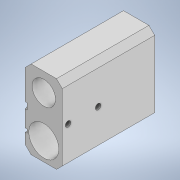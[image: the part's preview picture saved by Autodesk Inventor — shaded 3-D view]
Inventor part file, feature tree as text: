
AUTODESK INVENTOR PART (.ipt)
format: ipt  version: 2022 (Build 260153000, 153)  size: 282,624 bytes
history: native  units: in
note: dims shown in document units (in); Inventor stores cm internally (conversion verified against a paired STEP export)
features: extrude x5, sketch x4, projected_geometry x3, chamfer x1, fillet x1
ambient origin geometry x8: Origin, YZ Plane, XZ Plane, XY Plane, X Axis, Y Axis, Z Axis, Center Point
bodies: Solid1 (feature_tree)
feature tree (14):
  extrude  "Extrusion1"  Depth=0.6496in
  extrude  "Extrusion2"  Depth=1.7in
  chamfer  "Chamfer1"  Distance=2.0in
  sketch  "Sketch3"  dims[d4=0.8in d5=2.0in d6=0.0in]
  extrude  "Extrusion3"  Depth=0.0394in
  extrude  "Extrusion4"  Depth=0.0394in
  fillet  "Fillet1"  Radius=0.125in
  extrude  "Extrusion5"  Depth=0.25in TaperAngle=0.0deg
  sketch  "Sketch1"  dims[d0=0.5059in d1=0.6496in]
  sketch  "Sketch2"  dims[d2=0.9in d3=1.7in]
  projected_geometry  "Projected Loop1"
  projected_geometry  "Projected Loop2"
  sketch  "Sketch4"  dims[d7=0.12in d8=0.12in d9=0.65in d10=0.125in d11=0.25in d12=0.0in d13=0.125in d14=0.125in d15=45.0deg d18=0.5512in d19=0.0394in d20=0.0394in d21=0.0394in d22=0.0in d23=0.0787in d24=0.0in d25=0.125in d26=0.1575in d27=0.3937in d28=0.1575in d33=0.0394in d35=0.0787in d36=0.0394in d37=0.0787in d38=0.0394in d39=0.0in]
  projected_geometry  "Projected Loop3"
